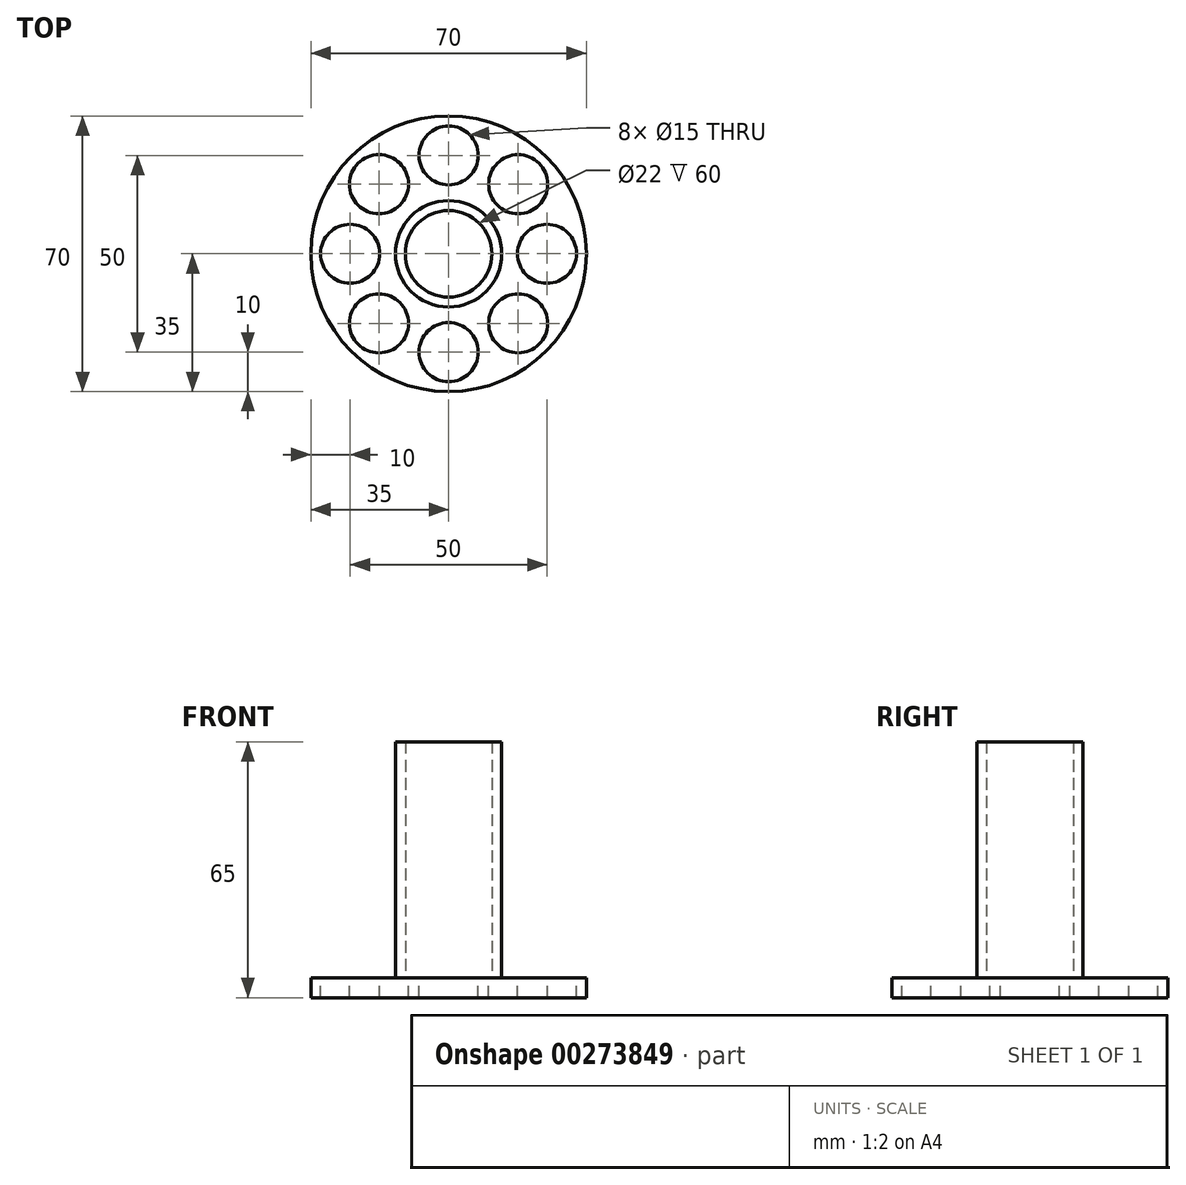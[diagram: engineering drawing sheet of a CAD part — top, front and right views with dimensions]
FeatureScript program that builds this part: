
annotation { "Feature Type Name" : "Feature", "Feature Type Description" : "" }
export const myFeature = defineFeature(function(context is Context, id is Id, definition is map)
    precondition{}
    {
        {
            var Q0;
            Q0=qCreatedBy(makeId("Top.planeOp"),FACE);
            var sketch = newSketch(context, id + "F0", { "sketchPlane" : qUnion([Q0])});
            skCircle(sketch, "E0", {"center": v(0, 0) * mm, "radius": 25 * mm, "construction": true});
            skCircle(sketch, "E1", {"center": v(0, 0) * mm, "radius": 11 * mm});
            skCircle(sketch, "E2", {"center": v(0, 0) * mm, "radius": 13.5 * mm});
            skCircle(sketch, "E3", {"center": v(0, 0) * mm, "radius": 35 * mm});
            skCircle(sketch, "E4", {"center": v(0, 25) * mm, "radius": 7.5 * mm});
            skCircle(sketch, "E5.1.0", {"center": v(-17.68, 17.68) * mm, "radius": 7.5 * mm});
            skCircle(sketch, "E5.2.0", {"center": v(-25, 0) * mm, "radius": 7.5 * mm});
            skCircle(sketch, "E5.3.0", {"center": v(-17.68, -17.68) * mm, "radius": 7.5 * mm});
            skCircle(sketch, "E5.4.0", {"center": v(0, -25) * mm, "radius": 7.5 * mm});
            skCircle(sketch, "E5.5.0", {"center": v(17.68, -17.68) * mm, "radius": 7.5 * mm});
            skCircle(sketch, "E5.6.0", {"center": v(25, 0) * mm, "radius": 7.5 * mm});
            skCircle(sketch, "E5.7.0", {"center": v(17.68, 17.68) * mm, "radius": 7.5 * mm});
            skSolve(sketch);
        }
        {
            var Q0;
            Q0=makeQuery(id+"F0.imprint","IMPRINT",FACE,{"disambiguationData":[TD([[makeQuery(id+"F0.imprint","IMPRINT",EDGE,{"derivedFrom":sQuery(id+"F0.wireOp",EDGE,"E2")}),-1.0]])]});
            var Q1;
            Q1=makeQuery(id+"F0.imprint","IMPRINT",FACE,{"disambiguationData":[TD([[makeQuery(id+"F0.imprint","IMPRINT",EDGE,{"derivedFrom":sQuery(id+"F0.wireOp",EDGE,"E1")}),-1.0]])]});
            var Q2;
            Q2=makeQuery(id+"F0.imprint","IMPRINT",FACE,{"disambiguationData":[TD([[makeQuery(id+"F0.imprint","IMPRINT",EDGE,{"derivedFrom":sQuery(id+"F0.wireOp",EDGE,"E1")}),1.0]])]});
            extrude(context, id + "F1", {"entities" : qUnion([Q0, Q1, Q2]), "oppositeDirection" : true, "depth" : 5 * mm});
        }
        {
            var Q0;
            Q0=makeQuery(id+"F0.imprint","IMPRINT",FACE,{"disambiguationData":[TD([[makeQuery(id+"F0.imprint","IMPRINT",EDGE,{"derivedFrom":sQuery(id+"F0.wireOp",EDGE,"E1")}),-1.0]])]});
            extrude(context, id + "F2", {"entities" : qUnion([Q0]), "operationType" : NewBodyOperationType.ADD, "depth" : 60 * mm});
        }
    });
